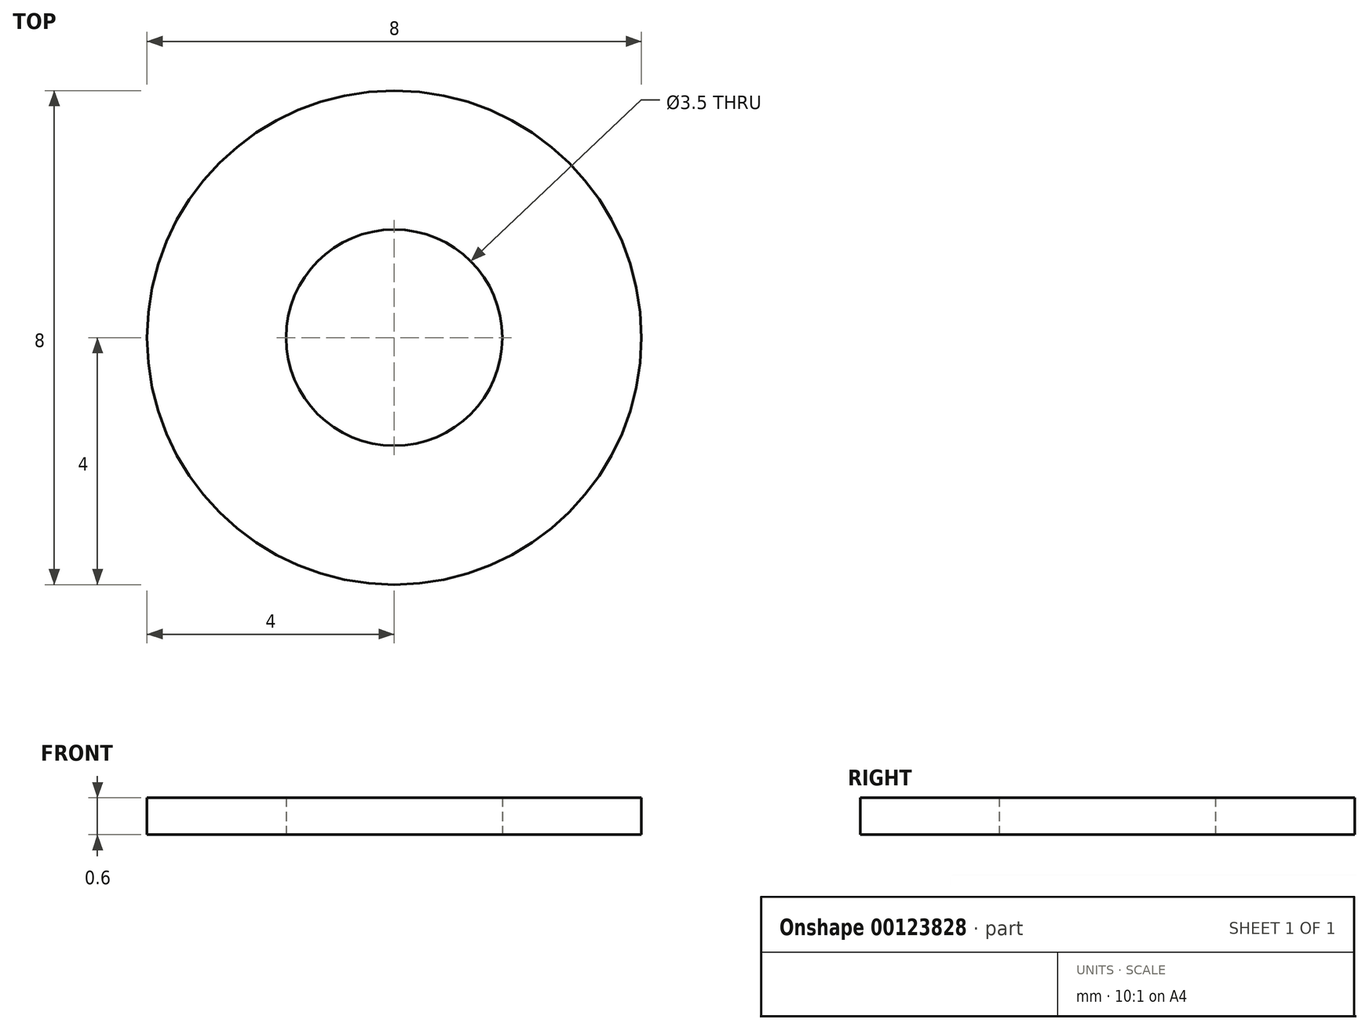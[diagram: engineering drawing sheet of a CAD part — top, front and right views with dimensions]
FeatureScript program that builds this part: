
annotation { "Feature Type Name" : "Feature", "Feature Type Description" : "" }
export const myFeature = defineFeature(function(context is Context, id is Id, definition is map)
    precondition{}
    {
        {
            var Q0;
            Q0=qCreatedBy(makeId("Top.planeOp"),FACE);
            var sketch = newSketch(context, id + "F0", { "sketchPlane" : qUnion([Q0])});
            skCircle(sketch, "E0", {"center": v(0, 0) * mm, "radius": 4 * mm});
            skCircle(sketch, "E1", {"center": v(0, 0) * mm, "radius": 1.75 * mm});
            skSolve(sketch);
        }
        {
            var Q0;
            Q0=makeQuery(id+"F0.imprint","IMPRINT",FACE,{"disambiguationData":[TD([[makeQuery(id+"F0.imprint","IMPRINT",EDGE,{"derivedFrom":sQuery(id+"F0.wireOp",EDGE,"E0")}),1.0]])]});
            extrude(context, id + "F1", {"entities" : qUnion([Q0]), "depth" : 0.6 * mm});
        }
    });
